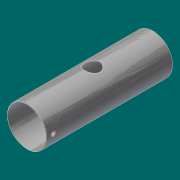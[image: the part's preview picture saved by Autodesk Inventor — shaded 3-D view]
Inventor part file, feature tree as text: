
AUTODESK INVENTOR PART (.ipt)
format: ipt  version: 2017.3 (Build 213257000, 257)  size: 235,520 bytes
history: native  units: in
note: dims shown in document units (in); Inventor stores cm internally (conversion verified against a paired STEP export)
features: extrude x7, split x5, other x5, sketch x4, plane x3, hole x3, pattern_circular x2, chamfer x2
ambient origin geometry x8: Origin, YZ Plane, XZ Plane, XY Plane, X Axis, Y Axis, Z Axis, Center Point
bodies: Solid1 (feature_tree)
feature tree (31):
  extrude  "Extrusion1"  Depth=33.0in
  plane  "Work Plane1"
  plane  "Work Plane2"
  sketch  "Sketch4"  dims[d2=108.7721in d3=0.0in d14=9.2291in]
  extrude  "Extrusion3"  Depth=108.7721in
  hole  "Hole1"  [1 undecoded]
  pattern_circular  "Circular Pattern1"  [2 undecoded]
  split  "Split1"
  split  "Split2"
  split  "Split3"
  split  "Split4"
  chamfer  "Chamfer1"  Distance=81.5359in
  hole  "Hole2"  [1 undecoded]
  pattern_circular  "Circular Pattern2"  [2 undecoded]
  plane  "Work Plane3"
  sketch  "Sketch6"  dims[d17=14.0in d18=46.9685in d19=81.5359in d20=0.0in d21=1.0in d22=0.0in d23=1.0in d24=0.0in d25=3.6875in d26=0.75in d27=0.375in d28=0.25in d29=0.5635in d30=1.0in d31=0.8108in d32=0.7874in d33=360.0deg d35=0.4375in d36=0.125in d37=0.2577in d38=12.8659in d39=0.891in d40=0.553in d41=0.0246in d42=0.897in d43=0.375in d44=0.25in d45=0.5635in d46=0.91in d47=0.8108in d48=1.1811in d49=135.0deg d51=4.125in d52=5.9063in d53=2.5625in d54=0.534in d55=0.375in d56=0.25in d57=0.5635in d58=0.891in d59=0.8108in d60=1.0in d61=0.0in d62=0.4375in d63=0.125in d64=0.2577in]
  hole  "Hole3"  [1 undecoded]
  split  "Split5"
  chamfer  "Chamfer2"  Distance=0.4375in
  sketch  "Sketch1"  dims[d0=34.0in d1=33.0in]
  other  "Srf1"
  other  "Srf2"
  other  "Srf3"
  other  "Srf4"
  sketch  "Sketch5"  dims[d15=5.25in d16=13.0in]
  other  "Srf5"
  extrude  "ExtrusionSrf1"  Depth=0.125in
  extrude  "ExtrusionSrf2"  Depth=12.8659in
  extrude  "ExtrusionSrf5"  Depth=1.1811in TaperAngle=135.0deg
  extrude  "ExtrusionSrf3"  Depth=4.125in
  extrude  "ExtrusionSrf4"  Depth=5.9063in
note: 7 required parameter values undecoded (feature->parameter linkage not recoverable at this tier; creation-order binding heuristic only, values carry confidence <= 0.55)
